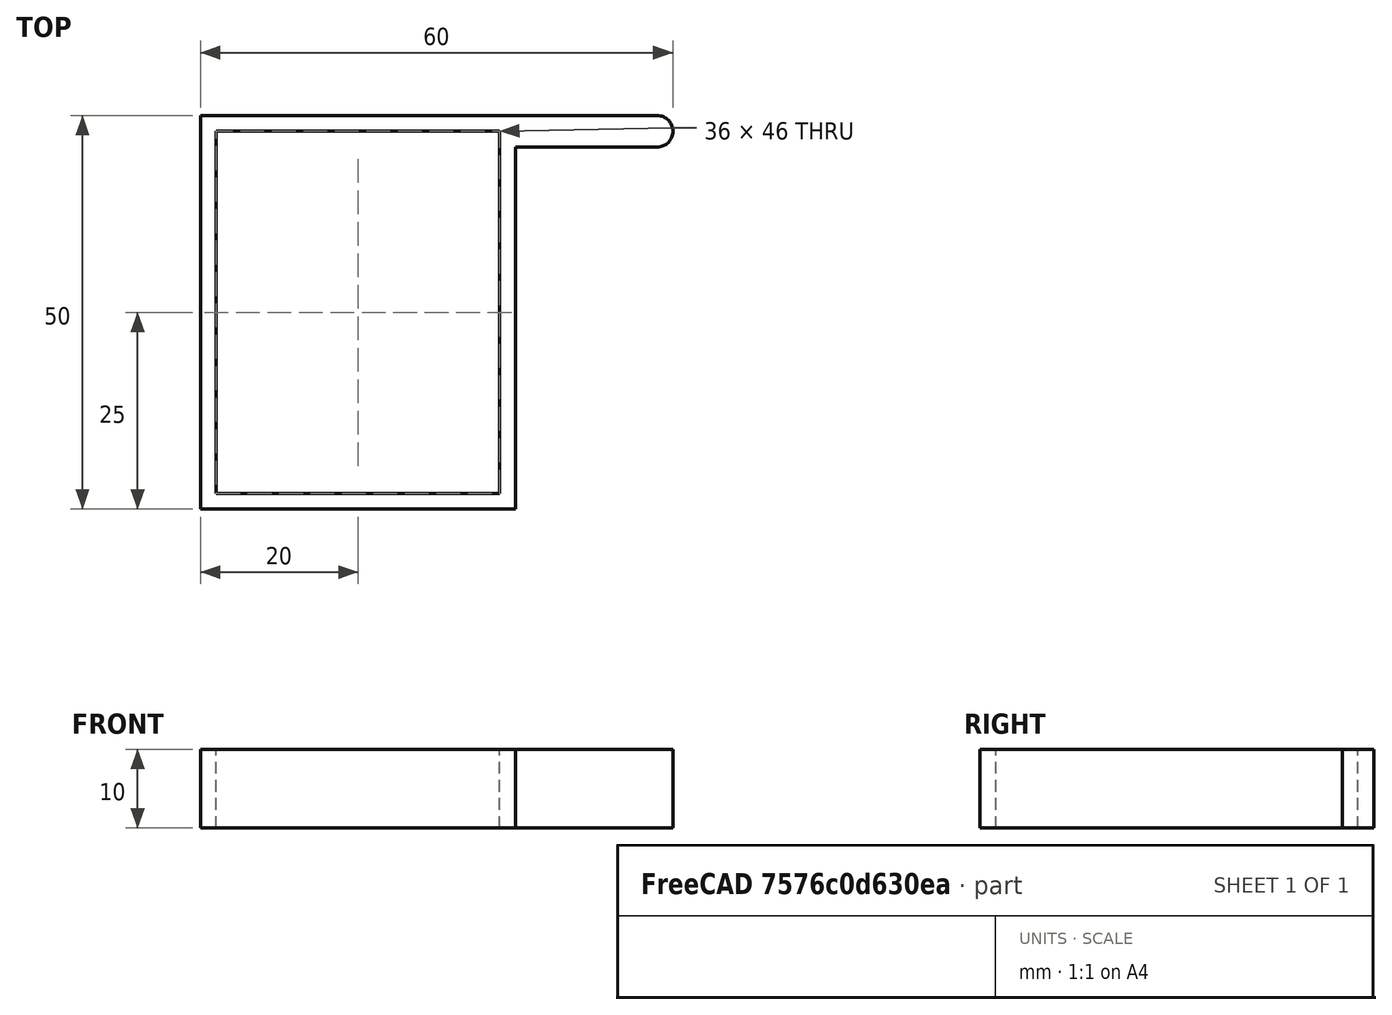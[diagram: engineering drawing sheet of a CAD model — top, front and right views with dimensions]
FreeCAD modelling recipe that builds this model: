
FCSTD DOCUMENT  (FreeCAD 0.17R13528 (Git))
Label: Perfil_R_5851
License: All rights reserved
LicenseURL: http://en.wikipedia.org/wiki/All_rights_reserved
objects: Spreadsheet::Sheet×1, Sketcher::SketchObject×1, PartDesign::Pad×1, PartDesign::Body×1
note: 4 computed .brp shape members not serialized (recipe doc carries the construction recipe); baked Part::Feature solids carry a one-line shape summary decoded from their .brp

FEATURE [Spreadsheet::Sheet] Spreadsheet  label="Tabla"
  cells = B1=Serie_A; C1=Serie_A; D1=Serie_B; E1=Serie_C; A2=Espesor; B2(Espesor_serie_A)=2; C2=1.5; D2=2; E2=2; A3=Alto; B3(Alto_serie_A)=50; C3=35; D3=50; E3=50; A4=Ancho; B4(Ancho_serie_A)=60; C4=30; D4=35; E4=60; A5=Ala; B5(Ala_serie_A)=20; C5=15; D5=15; E5=20
FEATURE [Sketcher::SketchObject] Sketch
  MapMode = 5
  Support = -> [XY_Plane]
  expr: Constraints[39] = Tabla.Ancho_serie_A - Tabla.Espesor_serie_A
  expr: Constraints[38] = Tabla.Ancho_serie_A - Tabla.Espesor_serie_A
  expr: Constraints[32] = Tabla.Ancho_serie_A
  expr: Constraints[37] = Tabla.Ala_serie_A - Tabla.Espesor_serie_A
  expr: Constraints[36] = Tabla.Alto_serie_A - Tabla.Espesor_serie_A * 2
  expr: Constraints[18] = Tabla.Alto_serie_A - 2 * Tabla.Espesor_serie_A
  expr: Constraints[33] = Tabla.Alto_serie_A
  expr: Constraints[20] = Tabla.Espesor_serie_A
  expr: Constraints[17] = Tabla.Espesor_serie_A
  expr: Constraints[19] = Tabla.Ancho_serie_A - Tabla.Ala_serie_A - 2 * Tabla.Espesor_serie_A
  expr: Constraints[7] = Tabla.Alto_serie_A
  expr: Constraints[8] = Tabla.Ancho_serie_A - Tabla.Ala_serie_A
  sketch-geometry (14):
    g0: LineSegment StartX=0 StartY=0 StartZ=0 EndX=0 EndY=50 EndZ=0
    g1: LineSegment StartX=0 StartY=50 StartZ=0 EndX=58 EndY=50 EndZ=0
    g2: LineSegment StartX=58 StartY=46 StartZ=0 EndX=40 EndY=46 EndZ=0
    g3: LineSegment StartX=40 StartY=46 StartZ=0 EndX=40 EndY=0 EndZ=0
    g4: LineSegment StartX=40 StartY=0 StartZ=0 EndX=0 EndY=0 EndZ=0
    g5: LineSegment StartX=2 StartY=48 StartZ=0 EndX=38 EndY=48 EndZ=0
    g6: LineSegment StartX=38 StartY=48 StartZ=0 EndX=38 EndY=2 EndZ=0
    g7: LineSegment StartX=38 StartY=2 StartZ=0 EndX=2 EndY=2 EndZ=0
    g8: LineSegment StartX=2 StartY=2 StartZ=0 EndX=2 EndY=48 EndZ=0
    g9: ArcOfCircle CenterX=58 CenterY=48 CenterZ=0 NormalX=0 NormalY=0 NormalZ=1 AngleXU=0 Radius=2 StartAngle=4.71239 EndAngle=7.85398
    g10: LineSegment [constr] StartX=0 StartY=0 StartZ=0 EndX=60 EndY=0 EndZ=0
    g11: LineSegment [constr] StartX=60 StartY=0 StartZ=0 EndX=60 EndY=50 EndZ=0
    g12: LineSegment [constr] StartX=60 StartY=50 StartZ=0 EndX=0 EndY=50 EndZ=0
    g13: LineSegment [constr] StartX=0 StartY=50 StartZ=0 EndX=0 EndY=0 EndZ=0
  constraints (41):
    c: Coincident(g-1,g0)
    c: Coincident(g0,g1)
    c: Coincident(g2,g3)
    c: PointOnObject(g3,g-1)
    c: Vertical(g3)
    c: Coincident(g3,g4)
    c: Coincident(g4,g0)
    c: DistanceY(g0,g0) = 50
    c: DistanceX(g4,g4) = 40
    c: Coincident(g5,g6)
    c: Coincident(g6,g7)
    c: Coincident(g7,g8)
    c: Coincident(g8,g5)
    c: Horizontal(g5)
    c: Horizontal(g7)
    c: Vertical(g6)
    c: Vertical(g8)
    c: DistanceX(g0,g7) = 2
    c: DistanceY(g6,g6) = 46
    c: DistanceX(g5,g5) = 36
    c: DistanceY(g0,g7) = 2
    c: Horizontal(g1)
    c: Coincident(g9,g1)
    c: Coincident(g10,g11)
    c: Coincident(g11,g12)
    c: Coincident(g12,g13)
    c: Coincident(g13,g10)
    c: Horizontal(g10)
    c: Horizontal(g12)
    c: Vertical(g11)
    c: Vertical(g13)
    c: Coincident(g10,g-1)
    c: DistanceX(g12,g12) = 60
    c: DistanceY(g11,g11) = 50
    c: Horizontal(g2)
    c: Vertical(g0)
    c: DistanceY(g3,g3) = 46
    c: DistanceX(g2,g2) = 18
    c: DistanceX(g0,g9) = 58
    c: DistanceX(g1,g1) = 58
    c: Coincident(g9,g2)
FEATURE [PartDesign::Pad] Pad
  Length = 10
  Length2 = 100
  Profile = -> Sketch
  Refine = true
  Type = 0
FEATURE [PartDesign::Body] Body  label="Seria_A"
  Group = -> [Sketch,Pad]
  Origin = -> Origin
  Tip = -> Pad
